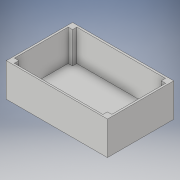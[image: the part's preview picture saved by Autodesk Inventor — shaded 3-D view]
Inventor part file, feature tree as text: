
AUTODESK INVENTOR PART (.ipt)
format: ipt  version: 2018 (Build 220112000, 112)  size: 123,904 bytes
history: native  units: in
note: dims shown in document units (in); Inventor stores cm internally (conversion verified against a paired STEP export)
features: sketch x3, extrude x2
ambient origin geometry x8: Origin, YZ Plane, XZ Plane, XY Plane, X Axis, Y Axis, Z Axis, Center Point
bodies: Solid1 (feature_tree)
feature tree (5):
  sketch  "Sketch1"  dims[d0=5.709in d1=3.74in]
  extrude  "Extrusion1"  Depth=3.74in
  extrude  "Extrusion2"  Depth=5.497in
  sketch  "Sketch2"  dims[d2=0.106in d3=0.0in d4=5.497in]
  sketch  "Sketch3"  dims[d5=3.528in d6=0.354in d7=0.354in d10=0.354in d11=0.354in d12=0.354in d13=0.354in d14=1.776in d15=0.0in]
